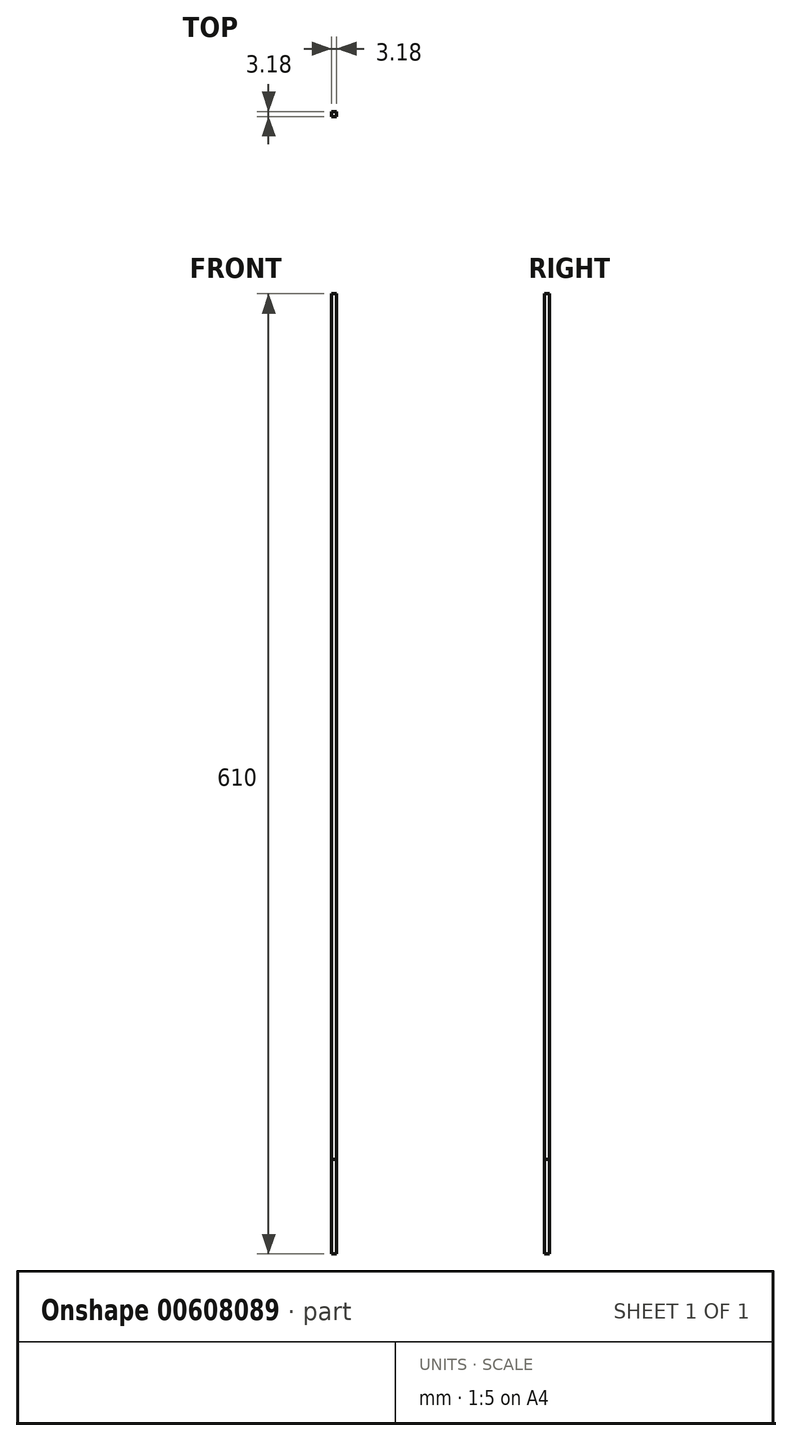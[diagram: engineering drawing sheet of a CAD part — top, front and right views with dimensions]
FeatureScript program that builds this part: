
annotation { "Feature Type Name" : "Feature", "Feature Type Description" : "" }
export const myFeature = defineFeature(function(context is Context, id is Id, definition is map)
    precondition{}
    {
        {
            var Q0;
            Q0=qCreatedBy(makeId("Top.planeOp"),FACE);
            var sketch = newSketch(context, id + "F0", { "sketchPlane" : qUnion([Q0])});
            skLineSegment(sketch, "E0.bottom", {"start": v(1.59, 1.59) * mm, "end": v(-1.59, 1.59) * mm});
            skLineSegment(sketch, "E0.top", {"start": v(1.59, -1.59) * mm, "end": v(-1.59, -1.59) * mm});
            skLineSegment(sketch, "E0.left", {"start": v(1.59, 1.59) * mm, "end": v(1.59, -1.59) * mm});
            skLineSegment(sketch, "E0.right", {"start": v(-1.59, 1.59) * mm, "end": v(-1.59, -1.59) * mm});
            skPoint(sketch, "E0.middle", {"position": v(0, 0) * mm});
            skSolve(sketch);
        }
        {
            var Q0;
            Q0=makeQuery(id+"F0.imprint","IMPRINT",FACE,{"disambiguationData":[TD([[makeQuery(id+"F0.imprint","IMPRINT",EDGE,{"derivedFrom":sQuery(id+"F0.wireOp",EDGE,"E0.bottom")}),1.0]])]});
            extrude(context, id + "F1", {"entities" : qUnion([Q0]), "depth" : 610 * mm, "offsetDistance" : 25 * mm});
        }
        {
            var Q0;
            Q0=makeQuery(id+"F0.imprint","IMPRINT",FACE,{"disambiguationData":[TD([[makeQuery(id+"F0.imprint","IMPRINT",EDGE,{"derivedFrom":sQuery(id+"F0.wireOp",EDGE,"E0.bottom")}),1.0]])]});
            extrude(context, id + "F2", {"entities" : qUnion([Q0]), "depth" : 60 * mm, "offsetDistance" : 25 * mm});
        }
    });
